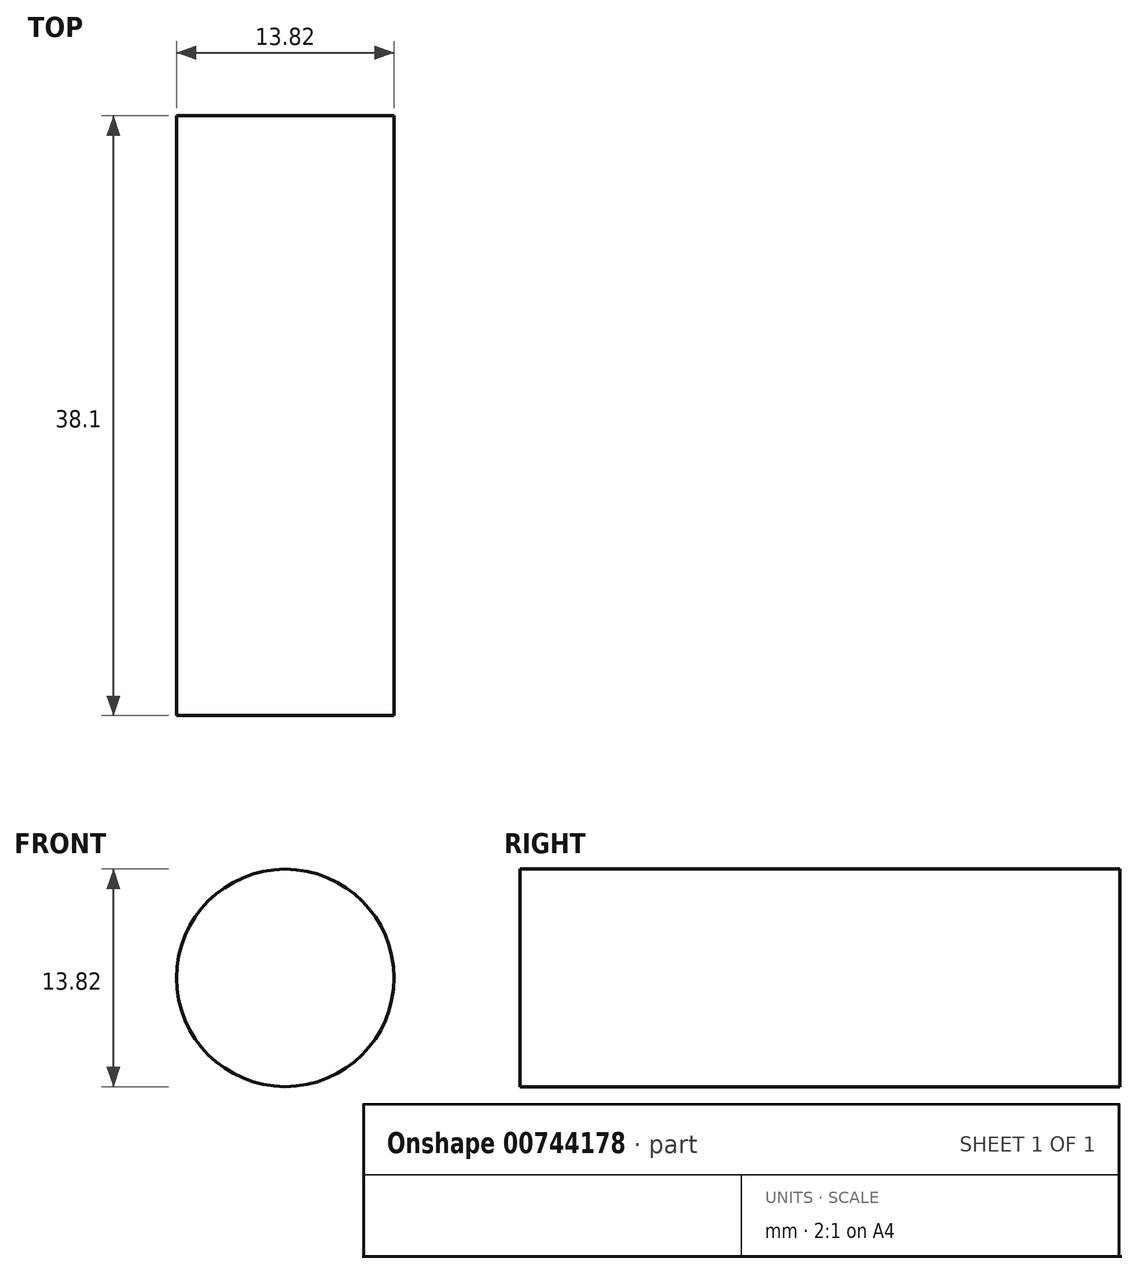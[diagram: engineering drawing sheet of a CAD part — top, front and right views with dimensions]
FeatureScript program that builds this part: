
annotation { "Feature Type Name" : "Feature", "Feature Type Description" : "" }
export const myFeature = defineFeature(function(context is Context, id is Id, definition is map)
    precondition{}
    {
        {
            var Q0;
            Q0=qCreatedBy(makeId("Front.planeOp"),FACE);
            var sketch = newSketch(context, id + "F0", { "sketchPlane" : qUnion([Q0])});
            skCircle(sketch, "E0", {"center": v(0, 0) * mm, "radius": 6.9 * mm});
            skSolve(sketch);
        }
        {
            var Q0;
            Q0=makeQuery(id+"F0.imprint","IMPRINT",FACE,{"disambiguationData":[TD([[makeQuery(id+"F0.imprint","IMPRINT",EDGE,{"derivedFrom":sQuery(id+"F0.wireOp",EDGE,"E0")}),1.0]])]});
            extrude(context, id + "F1", {"entities" : qUnion([Q0]), "depth" : 38.1 * mm, "offsetDistance" : 25.4 * mm});
        }
    });
